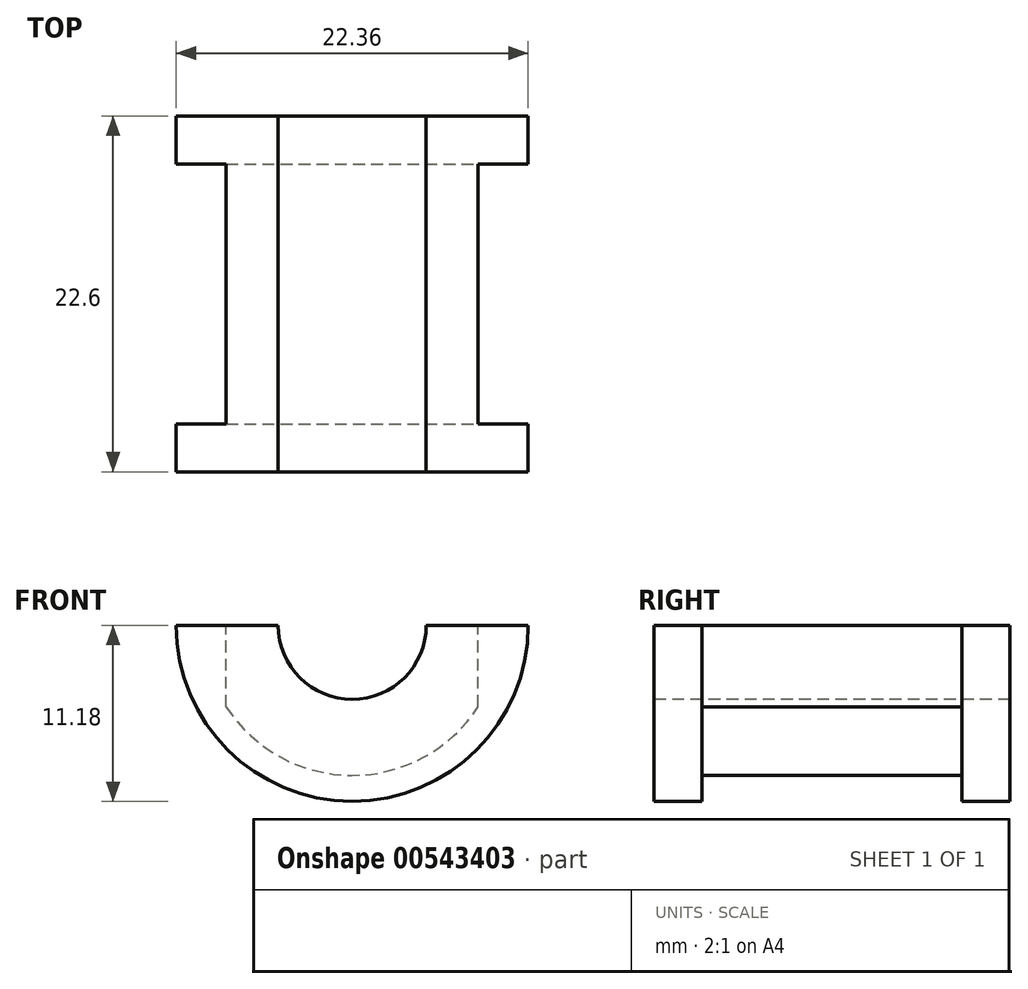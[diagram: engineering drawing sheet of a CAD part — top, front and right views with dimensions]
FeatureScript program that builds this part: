
annotation { "Feature Type Name" : "Feature", "Feature Type Description" : "" }
export const myFeature = defineFeature(function(context is Context, id is Id, definition is map)
    precondition{}
    {
        {
            var Q0;
            Q0=qCreatedBy(makeId("Right.planeOp"),FACE);
            var sketch = newSketch(context, id + "F0", { "sketchPlane" : qUnion([Q0])});
            skLineSegment(sketch, "E0", {"start": v(-23.35, 0) * mm, "end": v(24.13, 0) * mm, "construction": true});
            skLineSegment(sketch, "E1", {"start": v(-11.3, -4.7) * mm, "end": v(11.3, -4.7) * mm});
            skLineSegment(sketch, "E2", {"start": v(11.3, -4.7) * mm, "end": v(11.3, -11.18) * mm});
            skLineSegment(sketch, "E3", {"start": v(11.3, -11.18) * mm, "end": v(8.26, -11.18) * mm});
            skLineSegment(sketch, "E4", {"start": v(8.26, -11.18) * mm, "end": v(8.26, -9.53) * mm});
            skLineSegment(sketch, "E5", {"start": v(8.26, -9.53) * mm, "end": v(-8.26, -9.53) * mm});
            skLineSegment(sketch, "E6", {"start": v(-8.26, -9.53) * mm, "end": v(-8.26, -11.18) * mm});
            skLineSegment(sketch, "E7", {"start": v(-8.26, -11.18) * mm, "end": v(-11.3, -11.18) * mm});
            skLineSegment(sketch, "E8", {"start": v(-11.3, -11.18) * mm, "end": v(-11.3, -4.7) * mm});
            skSolve(sketch);
        }
        {
            var Q0;
            Q0 = qSketchRegion(id + "F0", true);
            var Q1;
            Q1=sQuery(id+"F0.wireOp",EDGE,"E0");
            revolve(context, id + "F1", {"entities" : qUnion([Q0]), "axis" : qUnion([Q1]), "revolveType" : RevolveType.SYMMETRIC, "angle" : 180 * degree});
        }
        {
            var Q0;
            Q0=makeQuery(id+"F1.opRevolve","CAP_FACE",FACE,{"disambiguationData":[OSD([sQuery(id+"F0.wireOp",EDGE,"E1"),sQuery(id+"F0.wireOp",EDGE,"E2"),sQuery(id+"F0.wireOp",EDGE,"E3"),sQuery(id+"F0.wireOp",EDGE,"E4"),sQuery(id+"F0.wireOp",EDGE,"E5"),sQuery(id+"F0.wireOp",EDGE,"E6"),sQuery(id+"F0.wireOp",EDGE,"E7"),sQuery(id+"F0.wireOp",EDGE,"E8")])],"isStart":true});
            var sketch = newSketch(context, id + "F2", { "sketchPlane" : qUnion([Q0])});
            skLineSegment(sketch, "E9.bottom", {"start": v(-9.52, 8.26) * mm, "end": v(-8, 8.26) * mm});
            skLineSegment(sketch, "E9.top", {"start": v(-9.53, -8.26) * mm, "end": v(-8, -8.26) * mm});
            skLineSegment(sketch, "E9.left", {"start": v(-9.53, 8.26) * mm, "end": v(-9.53, -8.26) * mm});
            skLineSegment(sketch, "E9.right", {"start": v(-8, 8.26) * mm, "end": v(-8, -8.26) * mm});
            skLineSegment(sketch, "E10.bottom", {"start": v(8, 8.26) * mm, "end": v(9.52, 8.26) * mm});
            skLineSegment(sketch, "E10.top", {"start": v(8, -8.26) * mm, "end": v(9.53, -8.26) * mm});
            skLineSegment(sketch, "E10.left", {"start": v(8, 8.26) * mm, "end": v(8, -8.26) * mm});
            skLineSegment(sketch, "E10.right", {"start": v(9.53, 8.26) * mm, "end": v(9.53, -8.26) * mm});
            skSolve(sketch);
        }
        {
            var Q0;
            Q0=makeQuery(id+"F2.imprint","IMPRINT",FACE,{"disambiguationData":[TD([[makeQuery(id+"F2.imprint","IMPRINT",EDGE,{"derivedFrom":sQuery(id+"F2.wireOp",EDGE,"E9.bottom")}),-1.0]])]});
            var Q1;
            Q1=makeQuery(id+"F2.imprint","IMPRINT",FACE,{"disambiguationData":[TD([[makeQuery(id+"F2.imprint","IMPRINT",EDGE,{"derivedFrom":sQuery(id+"F2.wireOp",EDGE,"E10.bottom")}),-1.0]])]});
            extrude(context, id + "F3", {"entities" : qUnion([Q0, Q1]), "operationType" : NewBodyOperationType.REMOVE, "endBound" : BoundingType.THROUGH_ALL, "oppositeDirection" : true, "depth" : 25.4 * mm, "offsetDistance" : 25.4 * mm});
        }
    });
